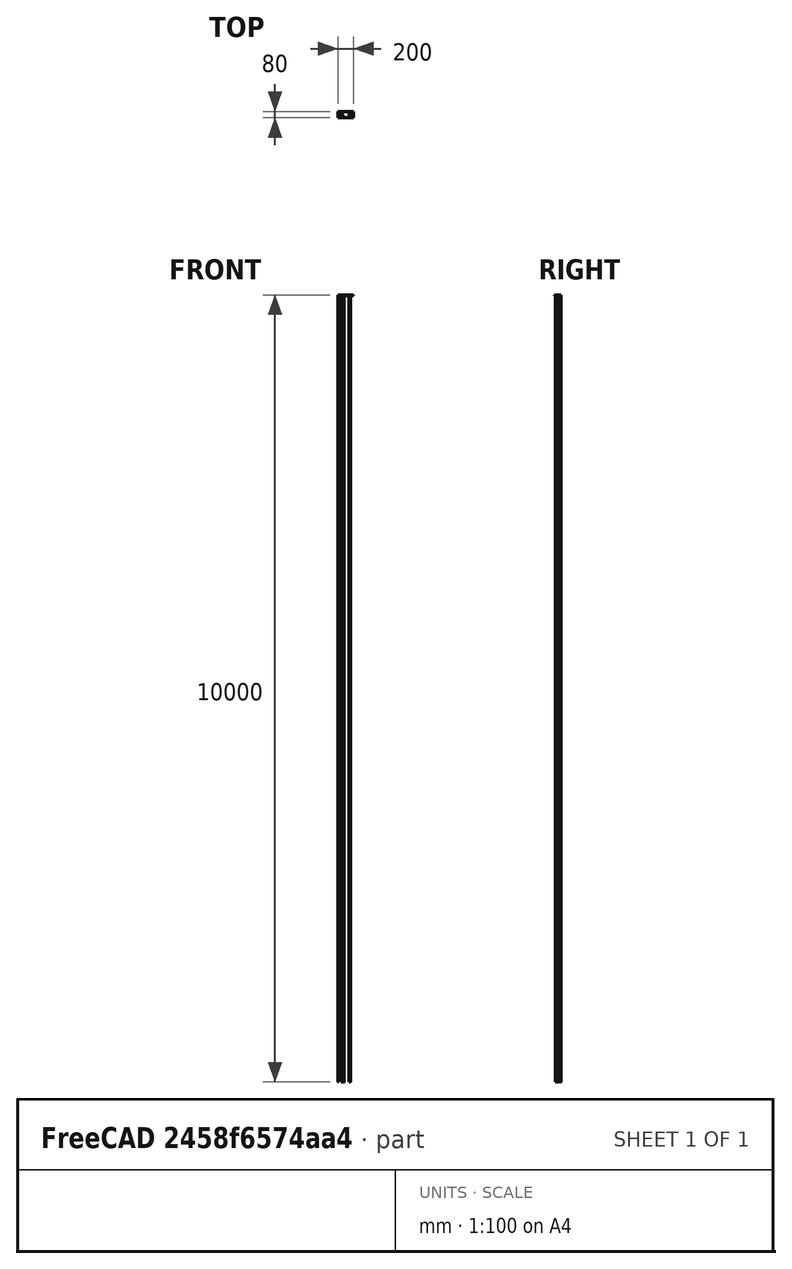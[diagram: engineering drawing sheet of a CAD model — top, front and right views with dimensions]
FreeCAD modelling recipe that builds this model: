
FCSTD DOCUMENT  (FreeCAD 0.14R3402 (Git))
Label: slide_rail_mount_right
License: CC-BY 3.0
LicenseURL: http://creativecommons.org/licenses/by/3.0/
objects: Mesh::Feature×8, Sketcher::SketchObject×2, PartDesign::Pocket×2, Part::Box×1
note: 7 computed .brp shape members not serialized (recipe doc carries the construction recipe); baked Part::Feature solids carry a one-line shape summary decoded from their .brp

FEATURE [Part::Box] Box  label="Cube"
  Height = 6
  Length = 200
  Width = 80
FEATURE [Sketcher::SketchObject] Sketch
  Placement = pos=(0,0,6) rot=(0,0,1;0rad)
  Support = -> Box [Face6]
  sketch-geometry (4):
    g0: Circle CenterX=50 CenterY=40 CenterZ=0 NormalX=0 NormalY=0 NormalZ=1 Radius=10.1
    g1: Circle CenterX=75 CenterY=15 CenterZ=0 NormalX=0 NormalY=0 NormalZ=1 Radius=6
    g2: Circle CenterX=150 CenterY=40 CenterZ=0 NormalX=0 NormalY=0 NormalZ=1 Radius=10.1
    g3: Circle CenterX=4.93925 CenterY=75.1029 CenterZ=0 NormalX=0 NormalY=0 NormalZ=1 Radius=2.5
  constraints (10):
    c: Radius(g0) = 10.1
    c: Radius(g1) = 6
    c: Equal(g0,g2)
    c: DistanceY(g-1,g2) = 40
    c: DistanceX(g-1,g0) = 50
    c: DistanceX(g1) = 75
    c: DistanceY(g-1,g1) = 15
    c: DistanceX(g2,g0) = -100
    c: DistanceY(g-1,g0) = 40
    c: Radius(g3) = 2.5
FEATURE [PartDesign::Pocket] Pocket
  Length = 5
  Sketch = -> Sketch
  Type = 1
FEATURE [Mesh::Feature] lm8uu_round_split_xnaron  label="lm8uu-round-split-xnaron"
  Placement = pos=(0,1,30) rot=(-1,0,0;1.5708rad)
FEATURE [Mesh::Feature] lm8uu_round_split_xnaron001  label="lm8uu-round-split-xnaron001"
  Placement = pos=(0,55,30) rot=(-1,0,0;1.5708rad)
FEATURE [Mesh::Feature] lm8uu_round_split_xnaron002  label="lm8uu-round-split-xnaron002"
  Placement = pos=(158,55,30) rot=(-1,0,0;1.5708rad)
FEATURE [Mesh::Feature] lm8uu_round_split_xnaron003  label="lm8uu-round-split-xnaron003"
  Placement = pos=(158,1,30) rot=(-1,0,0;1.5708rad)
FEATURE [Mesh::Feature] lm8uu_bearing
  Placement = pos=(20,1,18) rot=(0.57735,-0.57735,-0.57735;4.18879rad)
FEATURE [Mesh::Feature] lm8uu_bearing001
  Placement = pos=(20,55,18) rot=(0.57735,-0.57735,-0.57735;4.18879rad)
FEATURE [Mesh::Feature] lm8uu_bearing002
  Placement = pos=(179,55,18) rot=(0.57735,-0.57735,-0.57735;4.18879rad)
FEATURE [Mesh::Feature] lm8uu_bearing003
  Placement = pos=(179,1,18) rot=(0.57735,-0.57735,-0.57735;4.18879rad)
FEATURE [Sketcher::SketchObject] Sketch001
  Placement = pos=(0,0,6) rot=(0,0,1;0rad)
  Support = -> Box [Face6]
  sketch-geometry (4):
    g0: Circle CenterX=50 CenterY=40 CenterZ=0 NormalX=0 NormalY=0 NormalZ=1 Radius=10.1
    g1: Circle CenterX=75 CenterY=15 CenterZ=0 NormalX=0 NormalY=0 NormalZ=1 Radius=6
    g2: Circle CenterX=150 CenterY=40 CenterZ=0 NormalX=0 NormalY=0 NormalZ=1 Radius=10.1
    g3: Circle CenterX=4.93925 CenterY=75.1029 CenterZ=0 NormalX=0 NormalY=0 NormalZ=1 Radius=2.5
  constraints (10):
    c: Radius(g0) = 10.1
    c: Radius(g1) = 6
    c: Equal(g0,g2)
    c: DistanceY(g-1,g2) = 40
    c: DistanceX(g-1,g0) = 50
    c: DistanceX(g1) = 75
    c: DistanceY(g-1,g1) = 15
    c: DistanceX(g2,g0) = -100
    c: DistanceY(g-1,g0) = 40
    c: Radius(g3) = 2.5
FEATURE [PartDesign::Pocket] Pocket001
  Length = 5
  Sketch = -> Sketch001
  Type = 1
